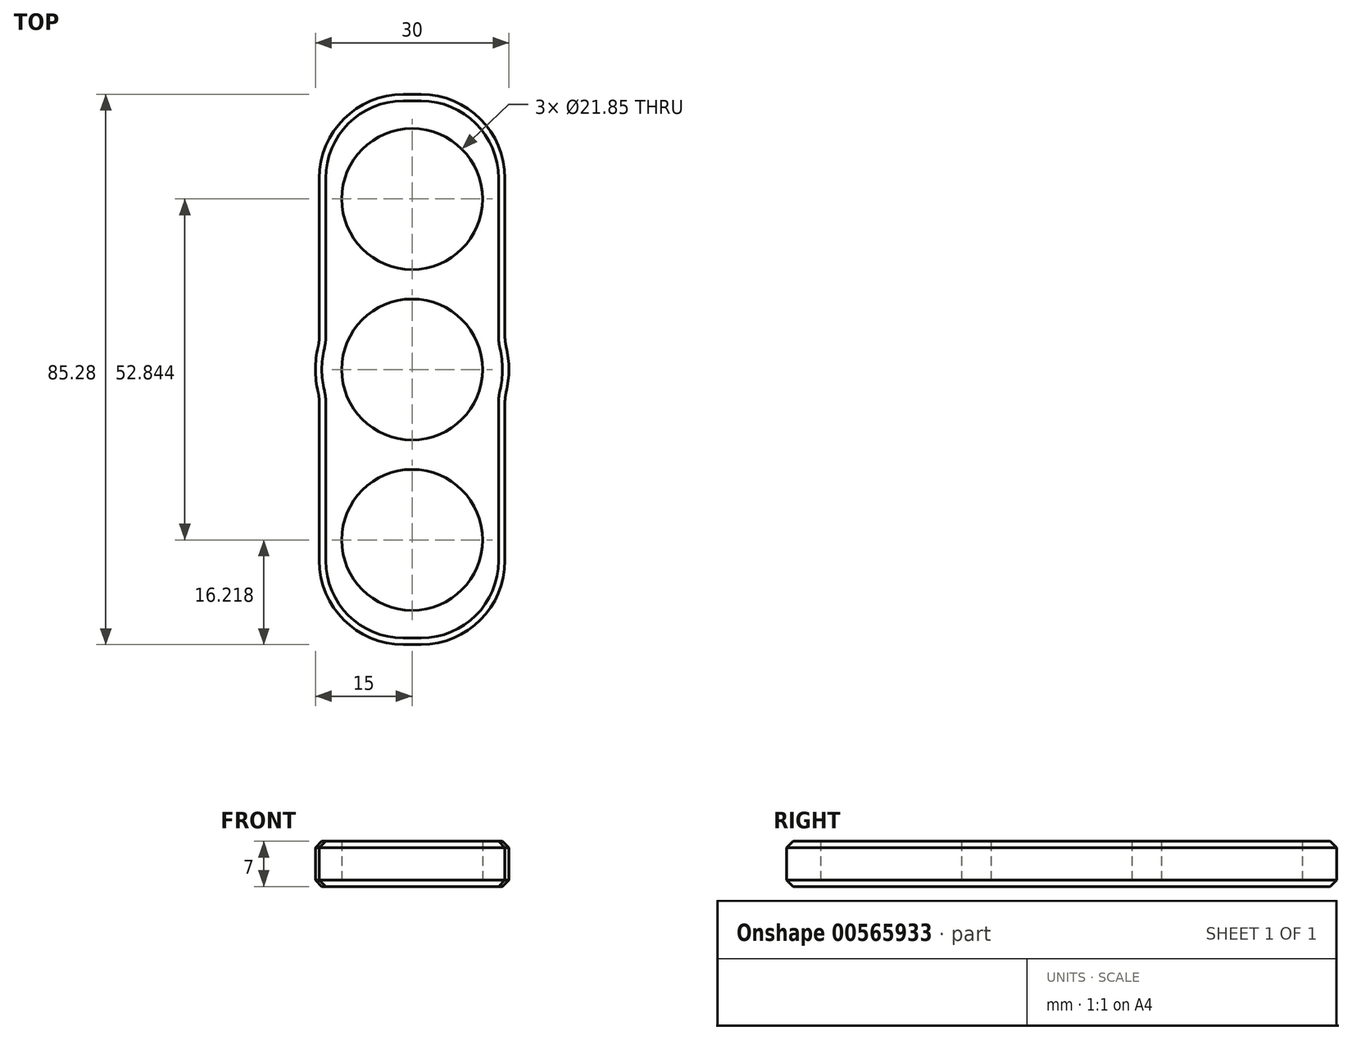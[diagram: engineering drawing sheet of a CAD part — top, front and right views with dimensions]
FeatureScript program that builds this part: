
annotation { "Feature Type Name" : "Feature", "Feature Type Description" : "" }
export const myFeature = defineFeature(function(context is Context, id is Id, definition is map)
    precondition{}
    {
        {
            var Q0;
            Q0=qCreatedBy(makeId("Top.planeOp"),FACE);
            var sketch = newSketch(context, id + "F0", { "sketchPlane" : qUnion([Q0])});
            skCircle(sketch, "E0", {"center": v(0, 0) * mm, "radius": 4 * mm});
            skCircle(sketch, "E1", {"center": v(0, 0) * mm, "radius": 10.93 * mm});
            skCircle(sketch, "E2", {"center": v(0, 0) * mm, "radius": 45 * mm, "construction": true});
            skCircle(sketch, "E3", {"center": v(0, 0) * mm, "radius": 15 * mm});
            skLineSegment(sketch, "E4", {"start": v(-14.39, 4.24) * mm, "end": v(-14.39, 42.64) * mm});
            skLineSegment(sketch, "E5.MirrorCS", {"start": v(14.39, 4.24) * mm, "end": v(14.39, 42.64) * mm});
            skLineSegment(sketch, "E6", {"start": v(-14.39, 42.64) * mm, "end": v(14.39, 42.64) * mm});
            skCircle(sketch, "E7", {"center": v(0, 26.42) * mm, "radius": 4 * mm});
            skCircle(sketch, "E8", {"center": v(0, 26.42) * mm, "radius": 10.93 * mm});
            skLineSegment(sketch, "E9.MirrorCS", {"start": v(-14.39, -4.24) * mm, "end": v(-14.39, -42.64) * mm});
            skCircle(sketch, "E10.MirrorC", {"center": v(0, -26.42) * mm, "radius": 10.93 * mm});
            skCircle(sketch, "E11.MirrorC", {"center": v(0, -26.42) * mm, "radius": 4 * mm});
            skLineSegment(sketch, "E12.MirrorCS", {"start": v(14.39, -4.24) * mm, "end": v(14.39, -42.64) * mm});
            skLineSegment(sketch, "E13.MirrorCS", {"start": v(-14.39, -42.64) * mm, "end": v(14.39, -42.64) * mm});
            skSolve(sketch);
        }
        {
            var Q0;
            {var subQ0=sQuery(id+"F0.wireOp",EDGE,"E4");Q0=makeQuery(id+"F0.imprint","IMPRINT",FACE,{"disambiguationData":[TD([[makeQuery(id+"F0.imprint","IMPRINT",EDGE,{"derivedFrom":subQ0}),-1.0]])]});}
            var Q1;
            Q1=makeQuery(id+"F0.imprint","IMPRINT",FACE,{"disambiguationData":[TD([[makeQuery(id+"F0.imprint","IMPRINT",EDGE,{"derivedFrom":sQuery(id+"F0.wireOp",EDGE,"E1")}),-1.0]])]});
            var Q2;
            {var subQ0=sQuery(id+"F0.wireOp",EDGE,"E9.MirrorCS");Q2=makeQuery(id+"F0.imprint","IMPRINT",FACE,{"disambiguationData":[TD([[makeQuery(id+"F0.imprint","IMPRINT",EDGE,{"derivedFrom":subQ0}),1.0]])]});}
            extrude(context, id + "F1", {"entities" : qUnion([Q0, Q1, Q2]), "endBound" : BoundingType.SYMMETRIC, "depth" : 7 * mm, "offsetDistance" : 25 * mm});
        }
        {
            var Q0;
            Q0=makeQuery(id+"F1.opExtrude","SWEPT_EDGE",EDGE,{"disambiguationData":[OSD([sQuery(id+"F0.wireOp",EDGE,"E4"),sQuery(id+"F0.wireOp",EDGE,"E6")])]});
            var Q1;
            Q1=makeQuery(id+"F1.opExtrude","SWEPT_EDGE",EDGE,{"disambiguationData":[OSD([sQuery(id+"F0.wireOp",EDGE,"E5.MirrorCS"),sQuery(id+"F0.wireOp",EDGE,"E6")])]});
            var Q2;
            Q2=makeQuery(id+"F1.opExtrude","SWEPT_EDGE",EDGE,{"disambiguationData":[OSD([sQuery(id+"F0.wireOp",EDGE,"E12.MirrorCS"),sQuery(id+"F0.wireOp",EDGE,"E13.MirrorCS")])]});
            var Q3;
            Q3=makeQuery(id+"F1.opExtrude","SWEPT_EDGE",EDGE,{"disambiguationData":[OSD([sQuery(id+"F0.wireOp",EDGE,"E9.MirrorCS"),sQuery(id+"F0.wireOp",EDGE,"E13.MirrorCS")])]});
            fillet(context, id + "F2", {"entities" : qUnion([Q0, Q1, Q2, Q3]), "radius" : 13 * mm, "tangentPropagation" : true, "allowEdgeOverflow" : false});
        }
        {
            var Q0;
            Q0=makeQuery(id+"F1.opExtrude","SWEPT_EDGE",EDGE,{"disambiguationData":[OSD([sQuery(id+"F0.wireOp",EDGE,"E3"),sQuery(id+"F0.wireOp",EDGE,"E12.MirrorCS")])]});
            var Q1;
            Q1=makeQuery(id+"F1.opExtrude","SWEPT_EDGE",EDGE,{"disambiguationData":[OSD([sQuery(id+"F0.wireOp",EDGE,"E3"),sQuery(id+"F0.wireOp",EDGE,"E5.MirrorCS")])]});
            var Q2;
            Q2=makeQuery(id+"F1.opExtrude","SWEPT_EDGE",EDGE,{"disambiguationData":[OSD([sQuery(id+"F0.wireOp",EDGE,"E3"),sQuery(id+"F0.wireOp",EDGE,"E4")])]});
            var Q3;
            Q3=makeQuery(id+"F1.opExtrude","SWEPT_EDGE",EDGE,{"disambiguationData":[OSD([sQuery(id+"F0.wireOp",EDGE,"E3"),sQuery(id+"F0.wireOp",EDGE,"E9.MirrorCS")])]});
            fillet(context, id + "F3", {"entities" : qUnion([Q0, Q1, Q2, Q3]), "radius" : 7 * mm, "tangentPropagation" : true, "allowEdgeOverflow" : false});
        }
        {
            var Q0;
            Q0=makeQuery(id+"F1.opExtrude","CAP_EDGE",EDGE,{"disambiguationData":[OSD([sQuery(id+"F0.wireOp",EDGE,"E12.MirrorCS")])],"isStart":false});
            var Q1;
            Q1=makeQuery(id+"F1.opExtrude","CAP_EDGE",EDGE,{"disambiguationData":[OSD([sQuery(id+"F0.wireOp",EDGE,"E12.MirrorCS")])],"isStart":true});
            chamfer(context, id + "F4", {"entities" : qUnion([Q0, Q1]), "width" : 1 * mm, "tangentPropagation" : true});
        }
    });
